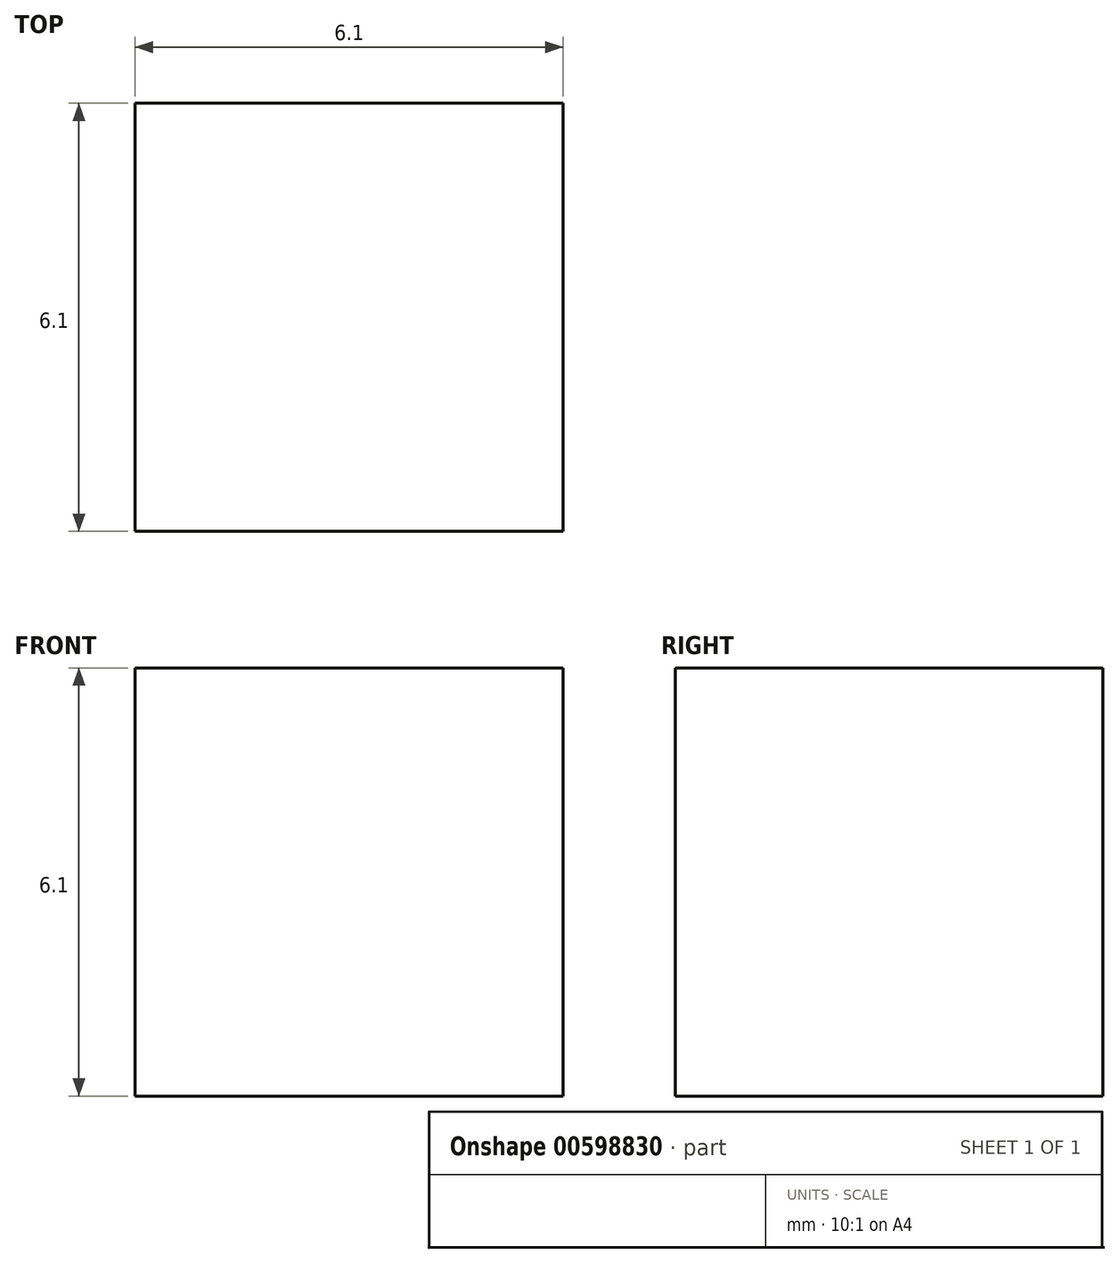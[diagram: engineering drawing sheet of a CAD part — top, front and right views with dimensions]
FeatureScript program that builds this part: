
annotation { "Feature Type Name" : "Feature", "Feature Type Description" : "" }
export const myFeature = defineFeature(function(context is Context, id is Id, definition is map)
    precondition{}
    {
        {
            var Q0;
            Q0=qCreatedBy(makeId("Top.planeOp"),FACE);
            var sketch = newSketch(context, id + "F0", { "sketchPlane" : qUnion([Q0])});
            skLineSegment(sketch, "E0.bottom", {"start": v(3.05, 3.05) * mm, "end": v(-3.05, 3.05) * mm});
            skLineSegment(sketch, "E0.top", {"start": v(3.05, -3.05) * mm, "end": v(-3.05, -3.05) * mm});
            skLineSegment(sketch, "E0.left", {"start": v(3.05, 3.05) * mm, "end": v(3.05, -3.05) * mm});
            skLineSegment(sketch, "E0.right", {"start": v(-3.05, 3.05) * mm, "end": v(-3.05, -3.05) * mm});
            skPoint(sketch, "E0.middle", {"position": v(0, 0) * mm});
            skSolve(sketch);
        }
        {
            var Q0;
            Q0 = qSketchRegion(id + "F0", true);
            extrude(context, id + "F1", {"entities" : qUnion([Q0]), "depth" : 6.1 * mm, "offsetDistance" : 25 * mm});
        }
    });
